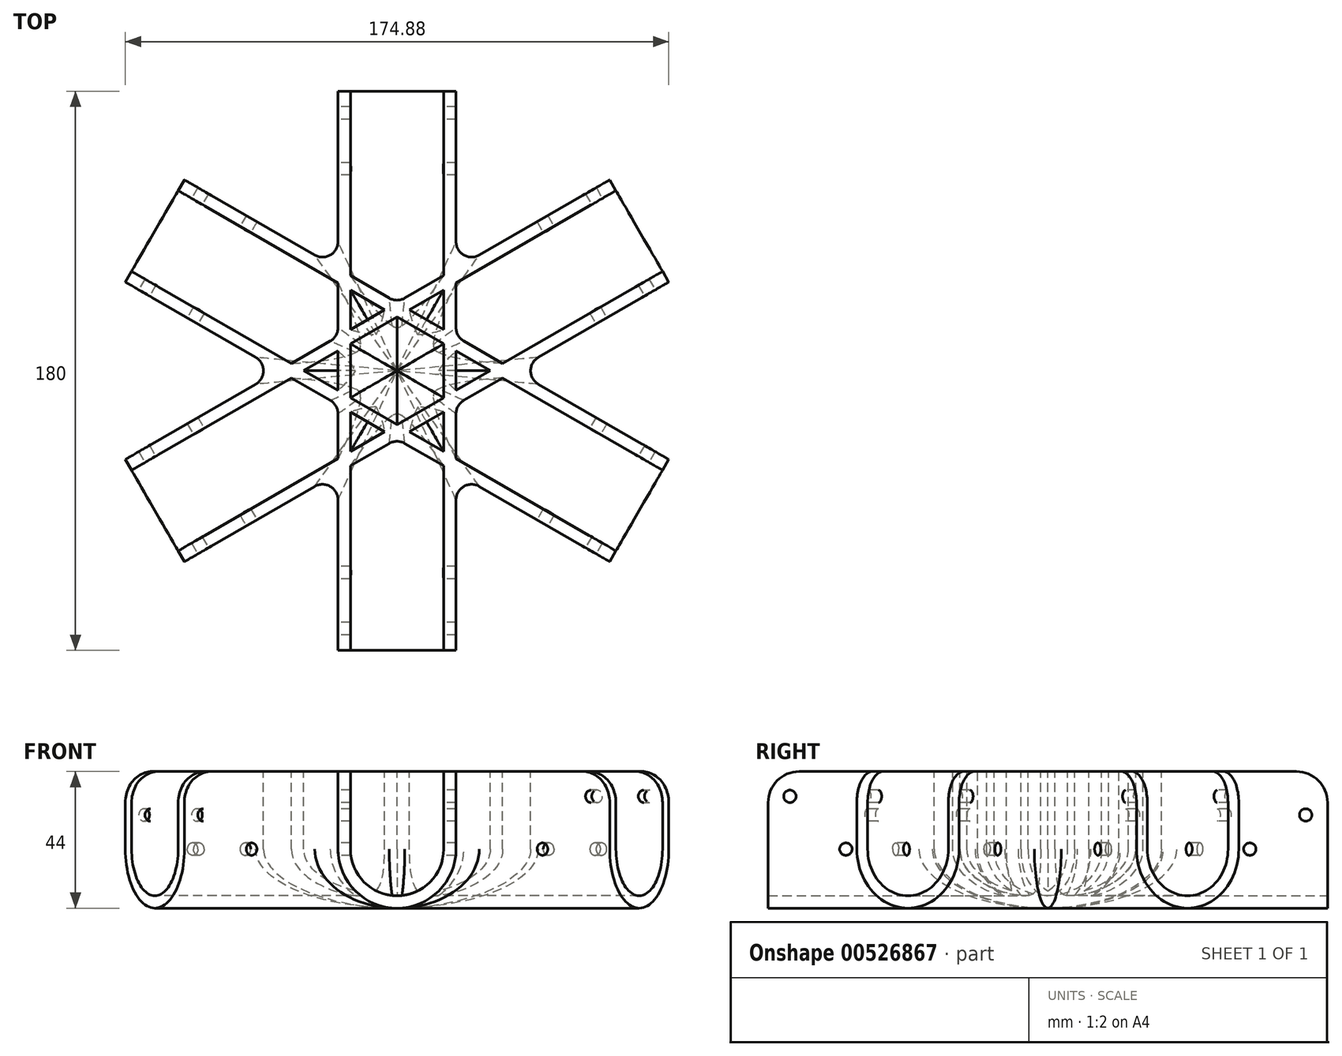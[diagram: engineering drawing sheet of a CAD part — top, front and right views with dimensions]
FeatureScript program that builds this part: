
annotation { "Feature Type Name" : "Feature", "Feature Type Description" : "" }
export const myFeature = defineFeature(function(context is Context, id is Id, definition is map)
    precondition{}
    {
        {
            var Q0;
            Q0=qCreatedBy(makeId("Front.planeOp"),FACE);
            var sketch = newSketch(context, id + "F0", { "sketchPlane" : qUnion([Q0])});
            skArc(sketch, "E0", {"start": v(-15, 0) * mm, "mid": v(0, -15) * mm, "end": v(15, 0) * mm});
            skLineSegment(sketch, "E1", {"start": v(-15, 0) * mm, "end": v(-15, 25) * mm});
            skLineSegment(sketch, "E2", {"start": v(15, 0) * mm, "end": v(15, 25) * mm});
            skLineSegment(sketch, "E3.0", {"start": v(-19, 0) * mm, "end": v(-19, 25) * mm});
            skArc(sketch, "E3.1", {"start": v(-19, 0) * mm, "mid": v(0, -19) * mm, "end": v(19, 0) * mm});
            skLineSegment(sketch, "E3.2", {"start": v(19, 0) * mm, "end": v(19, 25) * mm});
            skLineSegment(sketch, "E4", {"start": v(-19, 25) * mm, "end": v(-15, 25) * mm});
            skLineSegment(sketch, "E5", {"start": v(15, 25) * mm, "end": v(19, 25) * mm});
            skSolve(sketch);
        }
        {
            var Q0;
            Q0=makeQuery(id+"F0.imprint","IMPRINT",FACE,{"disambiguationData":[TD([[makeQuery(id+"F0.imprint","IMPRINT",EDGE,{"derivedFrom":sQuery(id+"F0.wireOp",EDGE,"E0")}),-1.0]])]});
            extrude(context, id + "F1", {"entities" : qUnion([Q0]), "depth" : 90 * mm, "offsetDistance" : 25 * mm, "hasSecondDirection" : true, "secondDirectionOppositeDirection" : true, "secondDirectionDepth" : 90 * mm});
        }
        {
            var Q0;
            Q0=makeQuery(id+"F1.opExtrude","SWEPT_FACE",FACE,{"disambiguationData":[OSD([sQuery(id+"F0.wireOp",EDGE,"E3.0")])]});
            var sketch = newSketch(context, id + "F2", { "sketchPlane" : qUnion([Q0])});
            skCircle(sketch, "E6", {"center": v(-83, 11) * mm, "radius": 2 * mm});
            skCircle(sketch, "E7", {"center": v(83, 17) * mm, "radius": 2 * mm});
            skCircle(sketch, "E8", {"center": v(-65, 0) * mm, "radius": 2 * mm});
            skCircle(sketch, "E9", {"center": v(65, 0) * mm, "radius": 2 * mm});
            skSolve(sketch);
        }
        {
            var Q0;
            Q0=makeQuery(id+"F2.imprint","IMPRINT",FACE,{"disambiguationData":[TD([[makeQuery(id+"F2.imprint","IMPRINT",EDGE,{"derivedFrom":sQuery(id+"F2.wireOp",EDGE,"E6")}),1.0]])]});
            var Q1;
            Q1=makeQuery(id+"F2.imprint","IMPRINT",FACE,{"disambiguationData":[TD([[makeQuery(id+"F2.imprint","IMPRINT",EDGE,{"derivedFrom":sQuery(id+"F2.wireOp",EDGE,"E7")}),1.0]])]});
            extrude(context, id + "F3", {"entities" : qUnion([Q0, Q1]), "operationType" : NewBodyOperationType.REMOVE, "endBound" : BoundingType.THROUGH_ALL, "oppositeDirection" : true, "depth" : 25 * mm, "offsetDistance" : 25 * mm});
        }
        {
            var Q0;
            {var subQ0=sQuery(id+"F2.wireOp",EDGE,"E8");var subQ1=makeQuery(id+"F1.opExtrude","SWEPT_EDGE",EDGE,{"disambiguationData":[OSD([sQuery(id+"F0.wireOp",EDGE,"E3.0"),sQuery(id+"F0.wireOp",EDGE,"E3.1")])]});var subQ2=makeQuery(id+"F2.imprint","INTERSECT",VERTEX,{"disambiguationData":[OD(0.0)],"derivedFrom":[subQ1,subQ0]});Q0=makeQuery(id+"F2.imprint","IMPRINT",FACE,{"disambiguationData":[TD([[makeQuery(id+"F2.imprint","IMPRINT",EDGE,{"disambiguationData":[TD([[subQ2,-1.0]])],"derivedFrom":subQ0}),1.0]])]});}
            var Q1;
            {var subQ0=sQuery(id+"F2.wireOp",EDGE,"E8");var subQ1=makeQuery(id+"F1.opExtrude","SWEPT_EDGE",EDGE,{"disambiguationData":[OSD([sQuery(id+"F0.wireOp",EDGE,"E3.0"),sQuery(id+"F0.wireOp",EDGE,"E3.1")])]});var subQ2=makeQuery(id+"F2.imprint","INTERSECT",VERTEX,{"disambiguationData":[OD(0.0)],"derivedFrom":[subQ1,subQ0]});Q1=makeQuery(id+"F2.imprint","IMPRINT",FACE,{"disambiguationData":[TD([[makeQuery(id+"F2.imprint","IMPRINT",EDGE,{"disambiguationData":[TD([[subQ2,1.0]])],"derivedFrom":subQ0}),1.0]])]});}
            var Q2;
            {var subQ0=sQuery(id+"F2.wireOp",EDGE,"E9");var subQ1=makeQuery(id+"F1.opExtrude","SWEPT_EDGE",EDGE,{"disambiguationData":[OSD([sQuery(id+"F0.wireOp",EDGE,"E3.0"),sQuery(id+"F0.wireOp",EDGE,"E3.1")])]});var subQ2=makeQuery(id+"F2.imprint","INTERSECT",VERTEX,{"disambiguationData":[OD(0.0)],"derivedFrom":[subQ1,subQ0]});Q2=makeQuery(id+"F2.imprint","IMPRINT",FACE,{"disambiguationData":[TD([[makeQuery(id+"F2.imprint","IMPRINT",EDGE,{"disambiguationData":[TD([[subQ2,1.0]])],"derivedFrom":subQ0}),1.0]])]});}
            var Q3;
            {var subQ0=sQuery(id+"F2.wireOp",EDGE,"E9");var subQ1=makeQuery(id+"F1.opExtrude","SWEPT_EDGE",EDGE,{"disambiguationData":[OSD([sQuery(id+"F0.wireOp",EDGE,"E3.0"),sQuery(id+"F0.wireOp",EDGE,"E3.1")])]});var subQ2=makeQuery(id+"F2.imprint","INTERSECT",VERTEX,{"disambiguationData":[OD(0.0)],"derivedFrom":[subQ1,subQ0]});Q3=makeQuery(id+"F2.imprint","IMPRINT",FACE,{"disambiguationData":[TD([[makeQuery(id+"F2.imprint","IMPRINT",EDGE,{"disambiguationData":[TD([[subQ2,-1.0]])],"derivedFrom":subQ0}),1.0]])]});}
            extrude(context, id + "F4", {"entities" : qUnion([Q0, Q1, Q2, Q3]), "operationType" : NewBodyOperationType.REMOVE, "endBound" : BoundingType.THROUGH_ALL, "oppositeDirection" : true, "depth" : 25 * mm, "offsetDistance" : 25 * mm});
        }
        {
            var Q0;
            Q0=makeQuery(id+"F1.opExtrude","CAP_EDGE",EDGE,{"disambiguationData":[OSD([sQuery(id+"F0.wireOp",EDGE,"E5")])],"isStart":true});
            var Q1;
            Q1=makeQuery(id+"F1.opExtrude","CAP_EDGE",EDGE,{"disambiguationData":[OSD([sQuery(id+"F0.wireOp",EDGE,"E4")])],"isStart":true});
            var Q2;
            Q2=makeQuery(id+"F1.opExtrude","CAP_EDGE",EDGE,{"disambiguationData":[OSD([sQuery(id+"F0.wireOp",EDGE,"E5")])],"isStart":false});
            var Q3;
            Q3=makeQuery(id+"F1.opExtrude","CAP_EDGE",EDGE,{"disambiguationData":[OSD([sQuery(id+"F0.wireOp",EDGE,"E4")])],"isStart":false});
            fillet(context, id + "F5", {"entities" : qUnion([Q0, Q1, Q2, Q3]), "radius" : 10 * mm, "tangentPropagation" : true, "allowEdgeOverflow" : false});
        }
        {
            var Q0;
            Q0=qCreatedBy(makeId("Front.planeOp"),FACE);
            var sketch = newSketch(context, id + "F6", { "sketchPlane" : qUnion([Q0])});
            skLineSegment(sketch, "E10", {"start": v(0, 0) * mm, "end": v(0, 63.73) * mm, "construction": true});
            skSolve(sketch);
        }
        {
            var Q0;
            Q0=makeQuery(id+"F1.opExtrude","SWEPT_BODY",BODY,{"disambiguationData":[OSD([sQuery(id+"F0.wireOp",EDGE,"E0"),sQuery(id+"F0.wireOp",EDGE,"E1"),sQuery(id+"F0.wireOp",EDGE,"E2"),sQuery(id+"F0.wireOp",EDGE,"E3.0"),sQuery(id+"F0.wireOp",EDGE,"E3.1"),sQuery(id+"F0.wireOp",EDGE,"E3.2"),sQuery(id+"F0.wireOp",EDGE,"E4"),sQuery(id+"F0.wireOp",EDGE,"E5")])]});
            var Q1;
            Q1=sQuery(id+"F6.wireOp",EDGE,"E10");
            circularPattern(context, id + "F7", {"operationType" : NewBodyOperationType.ADD, "entities" : qUnion([Q0]), "axis" : qUnion([Q1]), "angle" : 120 * degree, "instanceCount" : 3, "equalSpace" : true});
        }
        {
            var Q0;
            {var subQ0=makeQuery(id+"F1.opExtrude","SWEPT_FACE",FACE,{"disambiguationData":[OSD([sQuery(id+"F0.wireOp",EDGE,"E3.1")])]});Q0=makeQuery(id+"F7.boolean.opBoolean","INTERSECT",EDGE,{"disambiguationData":[OD(1.0)],"derivedFrom":[makeQuery(id+"F7.opPattern","COPY",FACE,{"derivedFrom":subQ0,"instanceName":"1"}),makeQuery(id+"F7.opPattern","COPY",FACE,{"derivedFrom":subQ0,"instanceName":"2"})]});}
            var Q1;
            {var subQ0=makeQuery(id+"F1.opExtrude","SWEPT_FACE",FACE,{"disambiguationData":[OSD([sQuery(id+"F0.wireOp",EDGE,"E3.1")])]});Q1=makeQuery(id+"F7.boolean.opBoolean","INTERSECT",EDGE,{"disambiguationData":[OD(0.0)],"derivedFrom":[subQ0,makeQuery(id+"F7.opPattern","COPY",FACE,{"derivedFrom":subQ0,"instanceName":"2"})]});}
            var Q2;
            {var subQ0=makeQuery(id+"F1.opExtrude","SWEPT_FACE",FACE,{"disambiguationData":[OSD([sQuery(id+"F0.wireOp",EDGE,"E3.1")])]});Q2=makeQuery(id+"F7.boolean.opBoolean","INTERSECT",EDGE,{"disambiguationData":[OD(0.0)],"derivedFrom":[makeQuery(id+"F7.opPattern","COPY",FACE,{"derivedFrom":subQ0,"instanceName":"1"}),makeQuery(id+"F7.opPattern","COPY",FACE,{"derivedFrom":subQ0,"instanceName":"2"})]});}
            var Q3;
            {var subQ0=makeQuery(id+"F1.opExtrude","SWEPT_FACE",FACE,{"disambiguationData":[OSD([sQuery(id+"F0.wireOp",EDGE,"E3.1")])]});Q3=makeQuery(id+"F7.boolean.opBoolean","INTERSECT",EDGE,{"disambiguationData":[OD(1.0)],"derivedFrom":[subQ0,makeQuery(id+"F7.opPattern","COPY",FACE,{"derivedFrom":subQ0,"instanceName":"2"})]});}
            var Q4;
            {var subQ0=makeQuery(id+"F1.opExtrude","SWEPT_FACE",FACE,{"disambiguationData":[OSD([sQuery(id+"F0.wireOp",EDGE,"E3.1")])]});Q4=makeQuery(id+"F7.boolean.opBoolean","INTERSECT",EDGE,{"disambiguationData":[OD(1.0)],"derivedFrom":[subQ0,makeQuery(id+"F7.opPattern","COPY",FACE,{"derivedFrom":subQ0,"instanceName":"1"})]});}
            var Q5;
            {var subQ0=makeQuery(id+"F1.opExtrude","SWEPT_FACE",FACE,{"disambiguationData":[OSD([sQuery(id+"F0.wireOp",EDGE,"E3.1")])]});Q5=makeQuery(id+"F7.boolean.opBoolean","INTERSECT",EDGE,{"disambiguationData":[OD(0.0)],"derivedFrom":[subQ0,makeQuery(id+"F7.opPattern","COPY",FACE,{"derivedFrom":subQ0,"instanceName":"1"})]});}
            fillet(context, id + "F8", {"entities" : qUnion([Q0, Q1, Q2, Q3, Q4, Q5]), "radius" : 5 * mm, "tangentPropagation" : true, "allowEdgeOverflow" : false});
        }
        {
            var Q0;
            Q0=qCreatedBy(makeId("Top.planeOp"),FACE);
            var sketch = newSketch(context, id + "F9", { "sketchPlane" : qUnion([Q0])});
            skLineSegment(sketch, "E11", {"start": v(-68.44, 61.45) * mm, "end": v(68.44, 61.45) * mm});
            skSolve(sketch);
        }
    });
